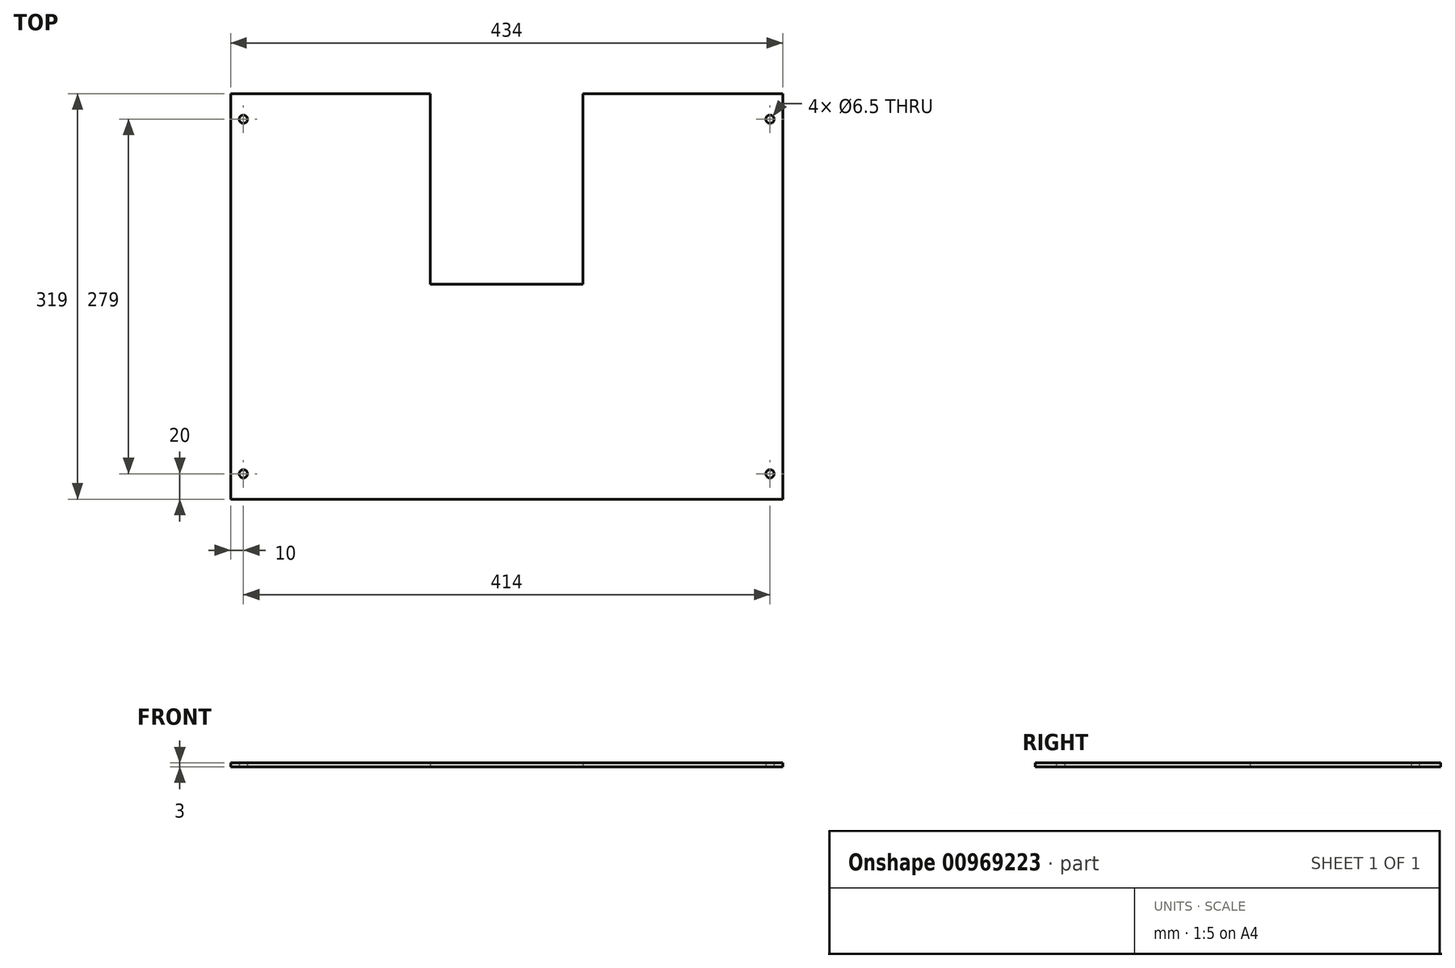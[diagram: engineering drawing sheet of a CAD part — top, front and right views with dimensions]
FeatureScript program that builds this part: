
annotation { "Feature Type Name" : "Feature", "Feature Type Description" : "" }
export const myFeature = defineFeature(function(context is Context, id is Id, definition is map)
    precondition{}
    {
        {
            var Q0;
            Q0=qCreatedBy(makeId("Top.planeOp"),FACE);
            var sketch = newSketch(context, id + "F0", { "sketchPlane" : qUnion([Q0])});
            skLineSegment(sketch, "E0.bottom", {"start": v(-217, 0) * mm, "end": v(-60, 0) * mm});
            skLineSegment(sketch, "E0.top", {"start": v(-217, -319) * mm, "end": v(217, -319) * mm});
            skLineSegment(sketch, "E0.left", {"start": v(-217, 0) * mm, "end": v(-217, -319) * mm});
            skLineSegment(sketch, "E0.right", {"start": v(217, 0) * mm, "end": v(217, -319) * mm});
            skLineSegment(sketch, "E1.top", {"start": v(-60, -150) * mm, "end": v(60, -150) * mm});
            skLineSegment(sketch, "E1.left", {"start": v(-60, 0) * mm, "end": v(-60, -150) * mm});
            skLineSegment(sketch, "E1.right", {"start": v(60, 0) * mm, "end": v(60, -150) * mm});
            skPoint(sketch, "E2", {"position": v(0, 0) * mm});
            skLineSegment(sketch, "E3.trimOffspring", {"start": v(60, 0) * mm, "end": v(217, 0) * mm});
            skCircle(sketch, "E4", {"center": v(-207, -20) * mm, "radius": 3.25 * mm});
            skCircle(sketch, "E5", {"center": v(-207, -299) * mm, "radius": 3.25 * mm});
            skCircle(sketch, "E6", {"center": v(207, -299) * mm, "radius": 3.25 * mm});
            skCircle(sketch, "E7", {"center": v(207, -20) * mm, "radius": 3.25 * mm});
            skSolve(sketch);
        }
        {
            var Q0;
            Q0 = qSketchRegion(id + "F0", true);
            extrude(context, id + "F1", {"entities" : qUnion([Q0]), "depth" : 3 * mm, "offsetDistance" : 25 * mm});
        }
    });
